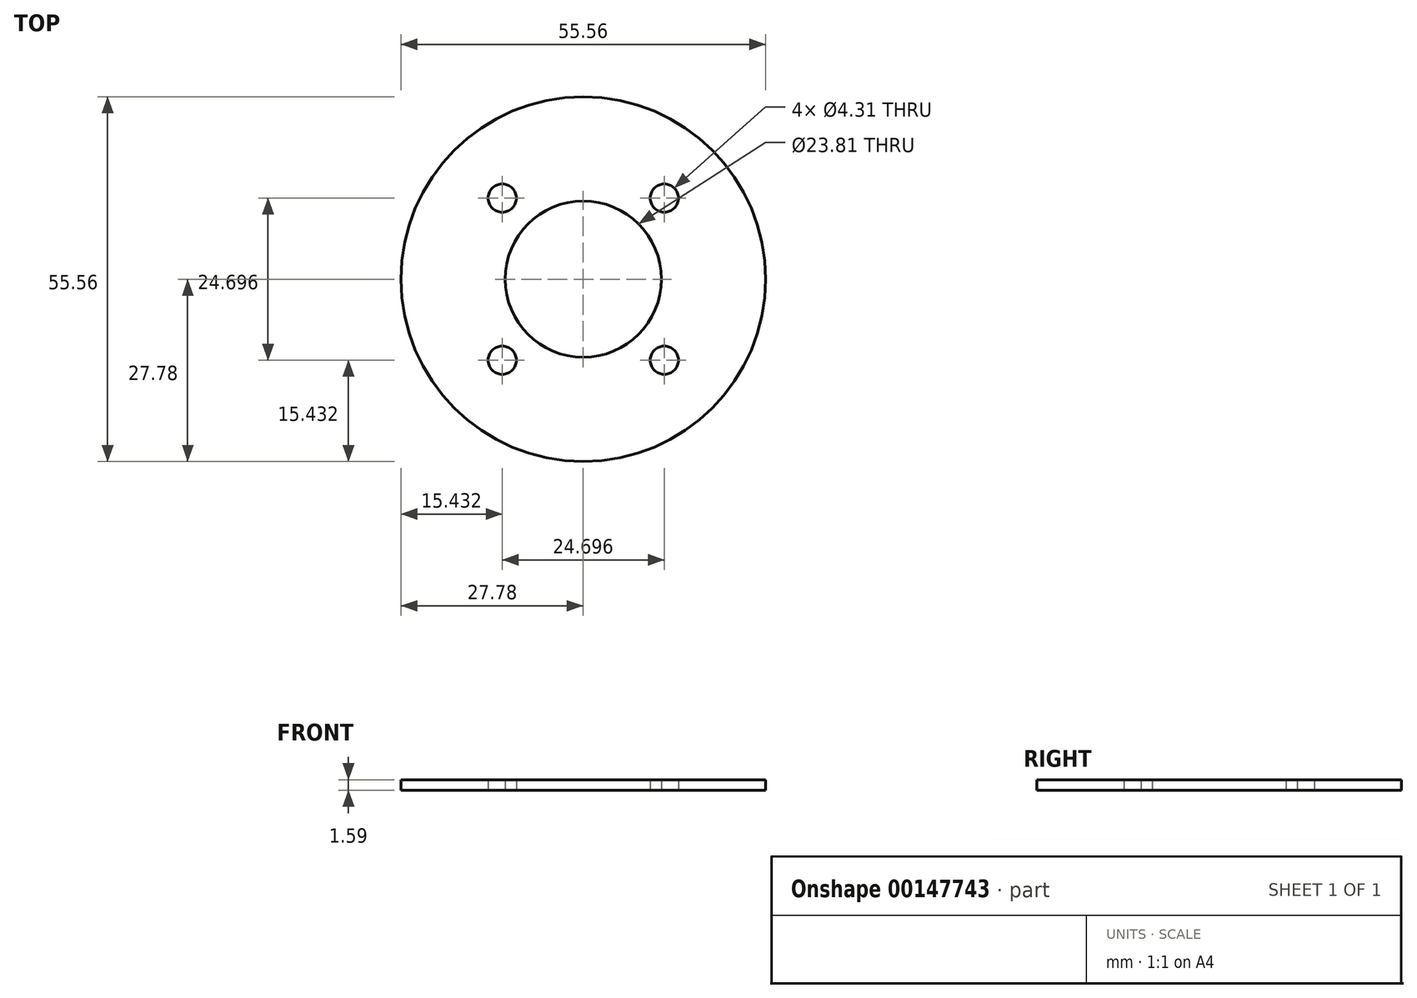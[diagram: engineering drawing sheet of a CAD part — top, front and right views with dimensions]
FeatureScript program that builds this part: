
annotation { "Feature Type Name" : "Feature", "Feature Type Description" : "" }
export const myFeature = defineFeature(function(context is Context, id is Id, definition is map)
    precondition{}
    {
        {
            var Q0;
            Q0=qCreatedBy(makeId("Top.planeOp"),FACE);
            var sketch = newSketch(context, id + "F0", { "sketchPlane" : qUnion([Q0])});
            skCircle(sketch, "E0", {"center": v(0, 0) * mm, "radius": 27.78 * mm});
            skCircle(sketch, "E1", {"center": v(0, 0) * mm, "radius": 11.9 * mm});
            skLineSegment(sketch, "E2.bottom", {"start": v(-12.35, 12.35) * mm, "end": v(12.35, 12.35) * mm, "construction": true});
            skLineSegment(sketch, "E2.top", {"start": v(-12.35, -12.35) * mm, "end": v(12.35, -12.35) * mm, "construction": true});
            skLineSegment(sketch, "E2.left", {"start": v(-12.35, 12.35) * mm, "end": v(-12.35, -12.35) * mm, "construction": true});
            skLineSegment(sketch, "E2.right", {"start": v(12.35, 12.35) * mm, "end": v(12.35, -12.35) * mm, "construction": true});
            skCircle(sketch, "E3", {"center": v(-12.35, 12.35) * mm, "radius": 5.56 * mm, "construction": true});
            skCircle(sketch, "E4", {"center": v(12.35, 12.35) * mm, "radius": 2.15 * mm});
            skCircle(sketch, "E5", {"center": v(-12.35, 12.35) * mm, "radius": 2.15 * mm});
            skCircle(sketch, "E6", {"center": v(-12.35, -12.35) * mm, "radius": 2.15 * mm});
            skCircle(sketch, "E7", {"center": v(12.35, -12.35) * mm, "radius": 2.15 * mm});
            skSolve(sketch);
        }
        {
            var Q0;
            Q0=qSketchRegion(id+"F0",true);
            extrude(context, id + "F1", {"entities" : qUnion([Q0]), "depth" : 1.59 * mm});
        }
    });
